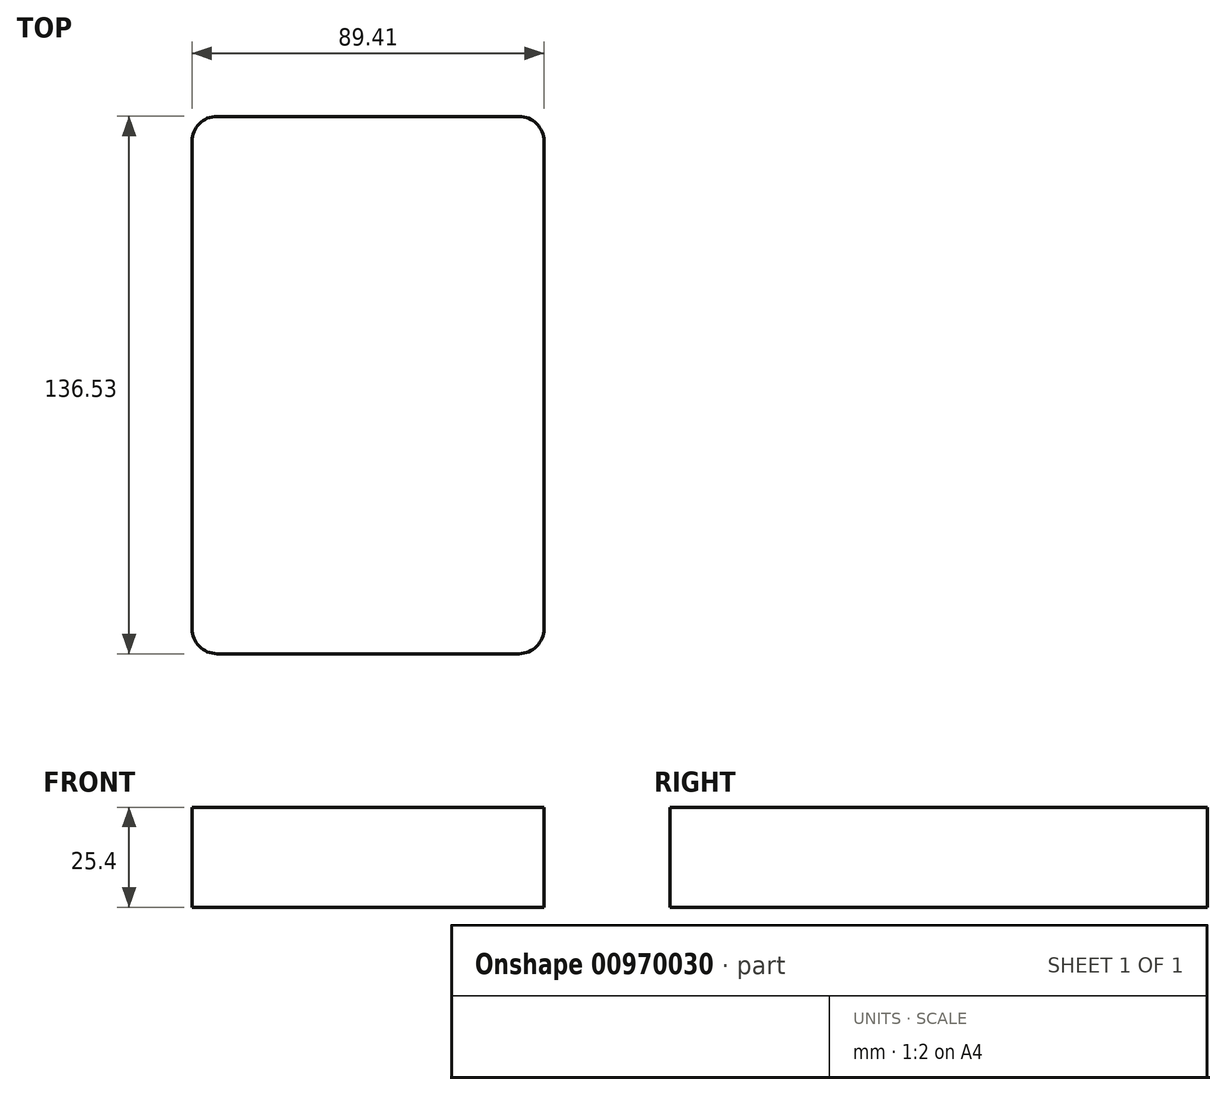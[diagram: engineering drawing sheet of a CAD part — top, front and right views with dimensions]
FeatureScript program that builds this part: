
annotation { "Feature Type Name" : "Feature", "Feature Type Description" : "" }
export const myFeature = defineFeature(function(context is Context, id is Id, definition is map)
    precondition{}
    {
        {
            var Q0;
            Q0=qCreatedBy(makeId("Top.planeOp"),FACE);
            var sketch = newSketch(context, id + "F0", { "sketchPlane" : qUnion([Q0])});
            skLineSegment(sketch, "E0.bottom", {"start": v(6.35, 0) * mm, "end": v(83.06, 0) * mm});
            skLineSegment(sketch, "E0.top", {"start": v(6.35, 136.53) * mm, "end": v(83.06, 136.53) * mm});
            skLineSegment(sketch, "E0.left", {"start": v(0, 6.35) * mm, "end": v(0, 130.18) * mm});
            skLineSegment(sketch, "E0.right", {"start": v(89.4, 6.35) * mm, "end": v(89.4, 130.18) * mm});
            skPoint(sketch, "E1.visualSharp", {"position": v(0, 136.53) * mm});
            skArc(sketch, "E1.filletArc", {"start": v(6.35, 136.53) * mm, "mid": v(1.86, 134.67) * mm, "end": v(0, 130.18) * mm});
            skPoint(sketch, "E2.visualSharp", {"position": v(89.4, 136.53) * mm});
            skArc(sketch, "E2.filletArc", {"start": v(89.4, 130.18) * mm, "mid": v(87.55, 134.67) * mm, "end": v(83.06, 136.53) * mm});
            skPoint(sketch, "E3.visualSharp", {"position": v(89.4, 0) * mm});
            skArc(sketch, "E3.filletArc", {"start": v(83.06, 0) * mm, "mid": v(87.55, 1.86) * mm, "end": v(89.4, 6.35) * mm});
            skPoint(sketch, "E4.visualSharp", {"position": v(0, 0) * mm});
            skArc(sketch, "E4.filletArc", {"start": v(0, 6.35) * mm, "mid": v(1.86, 1.86) * mm, "end": v(6.35, 0) * mm});
            skSolve(sketch);
        }
        {
            var Q0;
            Q0=makeQuery(id+"F0.imprint","IMPRINT",FACE,{"disambiguationData":[TD([[makeQuery(id+"F0.imprint","IMPRINT",EDGE,{"derivedFrom":sQuery(id+"F0.wireOp",EDGE,"E0.bottom")}),1.0]])]});
            extrude(context, id + "F1", {"entities" : qUnion([Q0]), "depth" : 25.4 * mm, "offsetDistance" : 25.4 * mm});
        }
    });
